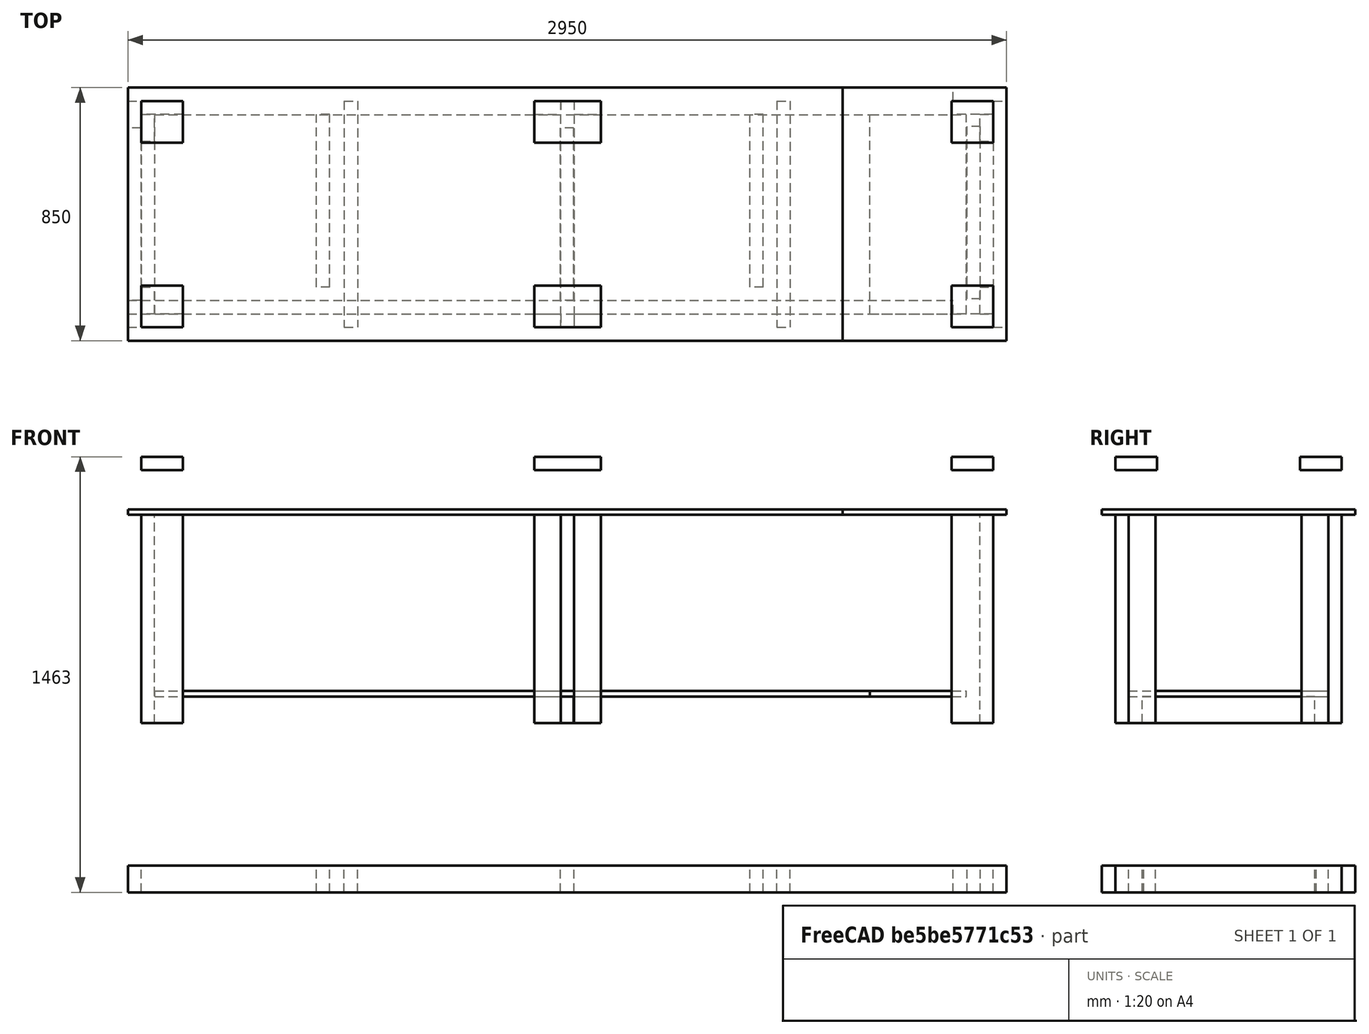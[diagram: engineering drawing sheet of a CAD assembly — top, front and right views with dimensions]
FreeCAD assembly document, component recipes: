
FREECAD ASSEMBLY — COMPONENT RECIPES ("Workbench")

This assembly document has 35 components, labeled P0..P34 below (a component is one placed body or linked part). 0 of them carry a construction recipe — the FreeCAD feature program that regenerates the part from scratch, quoted from this document or its linked companion documents; the rest are supplied as boundary geometry only. No exploded tour is included for this assembly.
COMPONENT P0 — geometry summary ("45x90x580 BASE005"; no construction recipe available for this part):
  bounding box: 580.0 x 90.0 x 45.0 mm
  tessellated surface: 12 triangles
  volume: 2349000 mm^3 (100% of its bounding box)
  symmetry: 2-fold rotationally symmetric about the x axis; 2-fold rotationally symmetric about the z axis; mirror-symmetric across its x mid-plane, z mid-plane
COMPONENT P1 — geometry summary ("45x90x2770 BASE003"; no construction recipe available for this part):
  bounding box: 2770.0 x 90.0 x 45.0 mm
  tessellated surface: 12 triangles
  volume: 11218500 mm^3 (100% of its bounding box)
  symmetry: 2-fold rotationally symmetric about the x axis; 2-fold rotationally symmetric about the y axis; 2-fold rotationally symmetric about the z axis; mirror-symmetric across its x mid-plane, y mid-plane, z mid-plane
COMPONENT P2 — geometry summary ("45x90x2770 BASE004"; no construction recipe available for this part):
  bounding box: 2770.0 x 90.0 x 45.0 mm
  tessellated surface: 12 triangles
  volume: 11218500 mm^3 (100% of its bounding box)
  symmetry: 2-fold rotationally symmetric about the x axis; 2-fold rotationally symmetric about the y axis; 2-fold rotationally symmetric about the z axis; mirror-symmetric across its x mid-plane, y mid-plane, z mid-plane
COMPONENT P3 — geometry summary ("45x90x580 BASE006"; no construction recipe available for this part):
  bounding box: 580.0 x 90.0 x 45.0 mm
  tessellated surface: 12 triangles
  volume: 2349000 mm^3 (100% of its bounding box)
  symmetry: 2-fold rotationally symmetric about the y axis; mirror-symmetric across its x mid-plane, y mid-plane, z mid-plane
COMPONENT P4 — geometry summary ("45x90x580 BASE007"; no construction recipe available for this part):
  bounding box: 580.0 x 90.0 x 45.0 mm
  tessellated surface: 12 triangles
  volume: 2349000 mm^3 (100% of its bounding box)
  symmetry: 2-fold rotationally symmetric about the y axis; mirror-symmetric across its x mid-plane, y mid-plane, z mid-plane
COMPONENT P5 — geometry summary ("45x90x580 BASE008"; no construction recipe available for this part):
  bounding box: 580.0 x 90.0 x 45.0 mm
  tessellated surface: 12 triangles
  volume: 2349000 mm^3 (100% of its bounding box)
  symmetry: 2-fold rotationally symmetric about the y axis; mirror-symmetric across its x mid-plane, y mid-plane, z mid-plane
COMPONENT P6 — geometry summary ("45x90x760 TOP006"; no construction recipe available for this part):
  bounding box: 760.0 x 90.0 x 45.0 mm
  tessellated surface: 12 triangles
  volume: 3078000 mm^3 (100% of its bounding box)
  symmetry: 2-fold rotationally symmetric about the y axis; 2-fold rotationally symmetric about the z axis; mirror-symmetric across its x mid-plane, y mid-plane, z mid-plane
COMPONENT P7 — geometry summary ("45x90x2950 TOP003"; no construction recipe available for this part):
  bounding box: 2950.0 x 90.0 x 45.0 mm
  tessellated surface: 12 triangles
  volume: 11947500 mm^3 (100% of its bounding box)
  symmetry: 2-fold rotationally symmetric about the x axis; 2-fold rotationally symmetric about the y axis; 2-fold rotationally symmetric about the z axis; mirror-symmetric across its x mid-plane, y mid-plane, z mid-plane
COMPONENT P8 — geometry summary ("45x90x2950 TOP004"; no construction recipe available for this part):
  bounding box: 2950.0 x 90.0 x 45.0 mm
  tessellated surface: 12 triangles
  volume: 11947500 mm^3 (100% of its bounding box)
  symmetry: 2-fold rotationally symmetric about the x axis; 2-fold rotationally symmetric about the y axis; 2-fold rotationally symmetric about the z axis; mirror-symmetric across its x mid-plane, y mid-plane, z mid-plane
COMPONENT P9 — geometry summary ("45x90x760 TOP007"; no construction recipe available for this part):
  bounding box: 760.0 x 90.0 x 45.0 mm
  tessellated surface: 12 triangles
  volume: 3078000 mm^3 (100% of its bounding box)
  symmetry: 2-fold rotationally symmetric about the y axis; 2-fold rotationally symmetric about the z axis; mirror-symmetric across its x mid-plane, y mid-plane, z mid-plane
COMPONENT P10 — geometry summary ("45x90x760 TOP008"; no construction recipe available for this part):
  bounding box: 760.0 x 90.0 x 45.0 mm
  tessellated surface: 12 triangles
  volume: 3078000 mm^3 (100% of its bounding box)
  symmetry: 2-fold rotationally symmetric about the y axis; 2-fold rotationally symmetric about the z axis; mirror-symmetric across its x mid-plane, y mid-plane, z mid-plane
COMPONENT P11 — geometry summary ("45x90x760 TOP009"; no construction recipe available for this part):
  bounding box: 760.0 x 90.0 x 45.0 mm
  tessellated surface: 12 triangles
  volume: 3078000 mm^3 (100% of its bounding box)
  symmetry: 2-fold rotationally symmetric about the y axis; 2-fold rotationally symmetric about the z axis; mirror-symmetric across its x mid-plane, y mid-plane, z mid-plane
COMPONENT P12 — geometry summary ("45x90x760 TOP010"; no construction recipe available for this part):
  bounding box: 760.0 x 90.0 x 45.0 mm
  tessellated surface: 12 triangles
  volume: 3078000 mm^3 (100% of its bounding box)
  symmetry: 2-fold rotationally symmetric about the y axis; 2-fold rotationally symmetric about the z axis; mirror-symmetric across its x mid-plane, y mid-plane, z mid-plane
COMPONENT P13 — geometry summary ("45x140x140 FOOT005"; no construction recipe available for this part):
  bounding box: 140.0 x 140.0 x 45.0 mm
  tessellated surface: 12 triangles
  volume: 882000 mm^3 (100% of its bounding box)
  symmetry: 2-fold rotationally symmetric about the x axis; 2-fold rotationally symmetric about the y axis; 4-fold rotationally symmetric about the z axis; mirror-symmetric across its x mid-plane, y mid-plane, z mid-plane
COMPONENT P14 — geometry summary ("45x140x140 FOOT006"; no construction recipe available for this part):
  bounding box: 140.0 x 140.0 x 45.0 mm
  tessellated surface: 12 triangles
  volume: 882000 mm^3 (100% of its bounding box)
  symmetry: 2-fold rotationally symmetric about the x axis; 2-fold rotationally symmetric about the y axis; 4-fold rotationally symmetric about the z axis; mirror-symmetric across its x mid-plane, y mid-plane, z mid-plane
COMPONENT P15 — geometry summary ("45x140x140 FOOT007"; no construction recipe available for this part):
  bounding box: 140.0 x 140.0 x 45.0 mm
  tessellated surface: 12 triangles
  volume: 882000 mm^3 (100% of its bounding box)
  symmetry: 2-fold rotationally symmetric about the x axis; 2-fold rotationally symmetric about the y axis; 4-fold rotationally symmetric about the z axis; mirror-symmetric across its x mid-plane, y mid-plane, z mid-plane
COMPONENT P16 — geometry summary ("45x140x140 FOOT008"; no construction recipe available for this part):
  bounding box: 140.0 x 140.0 x 45.0 mm
  tessellated surface: 12 triangles
  volume: 882000 mm^3 (100% of its bounding box)
  symmetry: 2-fold rotationally symmetric about the x axis; 2-fold rotationally symmetric about the y axis; 4-fold rotationally symmetric about the z axis; mirror-symmetric across its x mid-plane, y mid-plane, z mid-plane
COMPONENT P17 — geometry summary ("45x140x224 FOOT007"; no construction recipe available for this part):
  bounding box: 224.0 x 140.0 x 45.0 mm
  tessellated surface: 12 triangles
  volume: 1411200 mm^3 (100% of its bounding box)
  symmetry: 2-fold rotationally symmetric about the x axis; 2-fold rotationally symmetric about the y axis; mirror-symmetric across its x mid-plane, y mid-plane, z mid-plane
COMPONENT P18 — geometry summary ("45x140x224 FOOT008"; no construction recipe available for this part):
  bounding box: 224.0 x 140.0 x 45.0 mm
  tessellated surface: 12 triangles
  volume: 1411200 mm^3 (100% of its bounding box)
  symmetry: 2-fold rotationally symmetric about the x axis; 2-fold rotationally symmetric about the y axis; mirror-symmetric across its x mid-plane, y mid-plane, z mid-plane
COMPONENT P19 — geometry summary ("45x90x700 LEG009"; no construction recipe available for this part):
  bounding box: 700.0 x 90.0 x 45.0 mm
  tessellated surface: 12 triangles
  volume: 2835000 mm^3 (100% of its bounding box)
  symmetry: 2-fold rotationally symmetric about the x axis; mirror-symmetric across its y mid-plane, z mid-plane
COMPONENT P20 — geometry summary ("45x140x700 LEG005"; no construction recipe available for this part):
  bounding box: 700.0 x 140.0 x 45.0 mm
  tessellated surface: 12 triangles
  volume: 4410000 mm^3 (100% of its bounding box)
  symmetry: 2-fold rotationally symmetric about the x axis; 2-fold rotationally symmetric about the y axis; mirror-symmetric across its x mid-plane
COMPONENT P21 — geometry summary ("45x140x700 LEG006"; no construction recipe available for this part):
  bounding box: 700.0 x 140.0 x 45.0 mm
  tessellated surface: 12 triangles
  volume: 4410000 mm^3 (100% of its bounding box)
  symmetry: 2-fold rotationally symmetric about the x axis; 2-fold rotationally symmetric about the y axis; mirror-symmetric across its x mid-plane
COMPONENT P22 — geometry summary ("45x140x700 LEG007"; no construction recipe available for this part):
  bounding box: 700.0 x 140.0 x 45.0 mm
  tessellated surface: 12 triangles
  volume: 4410000 mm^3 (100% of its bounding box)
  symmetry: 2-fold rotationally symmetric about the x axis; 2-fold rotationally symmetric about the y axis; mirror-symmetric across its x mid-plane
COMPONENT P23 — geometry summary ("45x140x700 LEG008"; no construction recipe available for this part):
  bounding box: 700.0 x 140.0 x 45.0 mm
  tessellated surface: 12 triangles
  volume: 4410000 mm^3 (100% of its bounding box)
  symmetry: 2-fold rotationally symmetric about the x axis; 2-fold rotationally symmetric about the y axis; mirror-symmetric across its x mid-plane
COMPONENT P24 — geometry summary ("45x90x700 LEG010"; no construction recipe available for this part):
  bounding box: 700.0 x 90.0 x 45.0 mm
  tessellated surface: 12 triangles
  volume: 2835000 mm^3 (100% of its bounding box)
  symmetry: 2-fold rotationally symmetric about the y axis; mirror-symmetric across its x mid-plane, z mid-plane
COMPONENT P25 — geometry summary ("45x90x700 LEG011"; no construction recipe available for this part):
  bounding box: 700.0 x 90.0 x 45.0 mm
  tessellated surface: 12 triangles
  volume: 2835000 mm^3 (100% of its bounding box)
  symmetry: 2-fold rotationally symmetric about the y axis; mirror-symmetric across its x mid-plane, z mid-plane
COMPONENT P26 — geometry summary ("45x90x700 LEG012"; no construction recipe available for this part):
  bounding box: 700.0 x 90.0 x 45.0 mm
  tessellated surface: 12 triangles
  volume: 2835000 mm^3 (100% of its bounding box)
  symmetry: 2-fold rotationally symmetric about the y axis; mirror-symmetric across its x mid-plane, z mid-plane
COMPONENT P27 — geometry summary ("45x90x700 LEG013"; no construction recipe available for this part):
  bounding box: 700.0 x 90.0 x 45.0 mm
  tessellated surface: 12 triangles
  volume: 2835000 mm^3 (100% of its bounding box)
  symmetry: 2-fold rotationally symmetric about the y axis; mirror-symmetric across its x mid-plane, z mid-plane
COMPONENT P28 — geometry summary ("45x90x700 LEG014"; no construction recipe available for this part):
  bounding box: 700.0 x 90.0 x 45.0 mm
  tessellated surface: 12 triangles
  volume: 2835000 mm^3 (100% of its bounding box)
  symmetry: 2-fold rotationally symmetric about the x axis; mirror-symmetric across its y mid-plane, z mid-plane
COMPONENT P29 — geometry summary ("45x90x700 LEG015"; no construction recipe available for this part):
  bounding box: 700.0 x 90.0 x 45.0 mm
  tessellated surface: 12 triangles
  volume: 2835000 mm^3 (100% of its bounding box)
  symmetry: 2-fold rotationally symmetric about the x axis; mirror-symmetric across its y mid-plane, z mid-plane
COMPONENT P30 — geometry summary ("45x90x700 LEG016"; no construction recipe available for this part):
  bounding box: 700.0 x 90.0 x 45.0 mm
  tessellated surface: 12 triangles
  volume: 2835000 mm^3 (100% of its bounding box)
  symmetry: 2-fold rotationally symmetric about the x axis; mirror-symmetric across its y mid-plane, z mid-plane
COMPONENT P31 — geometry summary ("18x1200x550 MDF003"; no construction recipe available for this part):
  bounding box: 850.0 x 550.0 x 18.0 mm
  tessellated surface: 12 triangles
  volume: 8415000 mm^3 (100% of its bounding box)
  symmetry: 2-fold rotationally symmetric about the x axis; 2-fold rotationally symmetric about the y axis; mirror-symmetric across its x mid-plane
COMPONENT P32 — geometry summary ("18x1200x2400 MDF002"; no construction recipe available for this part):
  bounding box: 2400.0 x 850.0 x 18.0 mm
  tessellated surface: 12 triangles
  volume: 36720000 mm^3 (100% of its bounding box)
  symmetry: 2-fold rotationally symmetric about the x axis; 2-fold rotationally symmetric about the y axis; 2-fold rotationally symmetric about the z axis; mirror-symmetric across its x mid-plane, y mid-plane, z mid-plane
COMPONENT P33 — geometry summary ("18x670x279 MDF005"; no construction recipe available for this part):
  bounding box: 670.0 x 324.0 x 18.0 mm
  tessellated surface: 12 triangles
  volume: 3907440 mm^3 (100% of its bounding box)
  symmetry: 2-fold rotationally symmetric about the x axis; 2-fold rotationally symmetric about the y axis; 2-fold rotationally symmetric about the z axis; mirror-symmetric across its x mid-plane
COMPONENT P34 — geometry summary ("18x670x2400 MDF004"; no construction recipe available for this part):
  bounding box: 2400.0 x 670.0 x 18.0 mm
  tessellated surface: 12 triangles
  volume: 28944000 mm^3 (100% of its bounding box)
  symmetry: 2-fold rotationally symmetric about the x axis; 2-fold rotationally symmetric about the y axis; mirror-symmetric across its x mid-plane, y mid-plane, z mid-plane
PROVENANCE & LICENSES
A FreeCAD (.FCStd) document from a public repository crawl; recipes are the document's own serialized feature recipes (and, for linked parts, companion documents' recipes).
License: as declared in the source repository (recorded in the dataset sidecar).
